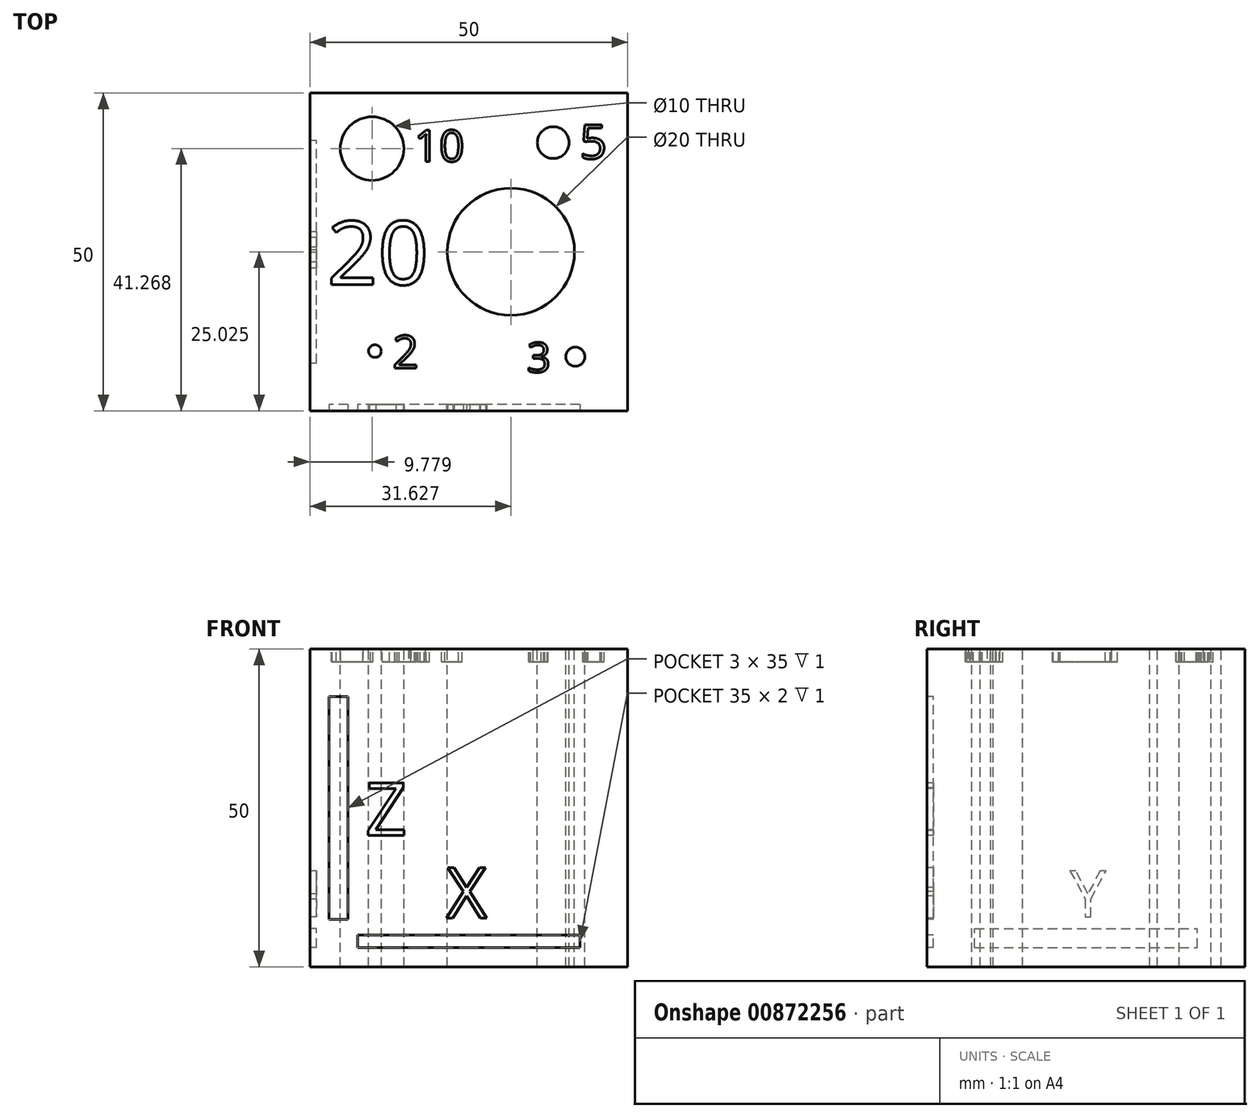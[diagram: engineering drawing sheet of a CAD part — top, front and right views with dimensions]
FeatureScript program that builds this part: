
annotation { "Feature Type Name" : "Feature", "Feature Type Description" : "" }
export const myFeature = defineFeature(function(context is Context, id is Id, definition is map)
    precondition{}
    {
        {
            var Q0;
            Q0=qCreatedBy(makeId("Top.planeOp"),FACE);
            var sketch = newSketch(context, id + "F0", { "sketchPlane" : qUnion([Q0])});
            skLineSegment(sketch, "E0.bottom", {"start": v(25, -25) * mm, "end": v(-25, -25) * mm});
            skLineSegment(sketch, "E0.top", {"start": v(25, 25) * mm, "end": v(-25, 25) * mm});
            skLineSegment(sketch, "E0.left", {"start": v(25, -25) * mm, "end": v(25, 25) * mm});
            skLineSegment(sketch, "E0.right", {"start": v(-25, -25) * mm, "end": v(-25, 25) * mm});
            skPoint(sketch, "E0.middle", {"position": v(0, 0) * mm});
            skSolve(sketch);
        }
        {
            var Q0;
            Q0 = qSketchRegion(id + "F0", true);
            extrude(context, id + "F1", {"entities" : qUnion([Q0]), "depth" : 50 * mm, "offsetDistance" : 25 * mm});
        }
        {
            var Q0;
            Q0=makeQuery(id+"F1.opExtrude","SWEPT_FACE",FACE,{"disambiguationData":[OSD([sQuery(id+"F0.wireOp",EDGE,"E0.bottom")])]});
            var sketch = newSketch(context, id + "F2", { "sketchPlane" : qUnion([Q0])});
            skLineSegment(sketch, "E1.bottom", {"start": v(17.5, 3) * mm, "end": v(-17.5, 3) * mm});
            skLineSegment(sketch, "E1.top", {"start": v(17.5, 5) * mm, "end": v(-17.5, 5) * mm});
            skLineSegment(sketch, "E1.left", {"start": v(17.5, 3) * mm, "end": v(17.5, 5) * mm});
            skLineSegment(sketch, "E1.right", {"start": v(-17.5, 3) * mm, "end": v(-17.5, 5) * mm});
            skPoint(sketch, "E1.middle", {"position": v(0, 4) * mm});
            skLineSegment(sketch, "E2.bottom", {"start": v(-19, 7.5) * mm, "end": v(-22, 7.5) * mm});
            skLineSegment(sketch, "E2.top", {"start": v(-19, 42.5) * mm, "end": v(-22, 42.5) * mm});
            skLineSegment(sketch, "E2.left", {"start": v(-19, 7.5) * mm, "end": v(-19, 42.5) * mm});
            skLineSegment(sketch, "E2.right", {"start": v(-22, 7.5) * mm, "end": v(-22, 42.5) * mm});
            skPoint(sketch, "E2.middle", {"position": v(-20.5, 25) * mm});
            skPoint(sketch, "E2.middle.positionSnap0", {"position": v(-25, 25) * mm});
            skPoint(sketch, "E2.centerSnap0", {"position": v(-25, 25) * mm});
            skText(sketch, "E3", { "text": "Z", "fontName": "OpenSans-Regular.ttf"});
            skText(sketch, "E4", { "text": "X", "fontName": "OpenSans-Regular.ttf"});
            skLineSegment(sketch, "E5", {"start": v(-25, 25) * mm, "end": v(25, 25) * mm, "construction": true});
            const initialGuessF2  = {"E3": [-0.01628, 0.02067, 1, 0, 0.0083], "E4": [-0.00355, 0.00767, 1, 0, 0.00801]};
            skSetInitialGuess(sketch, initialGuessF2);
            skSolve(sketch);
        }
        {
            var Q0;
            Q0=makeQuery(id+"F1.opExtrude","SWEPT_FACE",FACE,{"disambiguationData":[OSD([sQuery(id+"F0.wireOp",EDGE,"E0.right")])]});
            var sketch = newSketch(context, id + "F3", { "sketchPlane" : qUnion([Q0])});
            skLineSegment(sketch, "E6.bottom", {"start": v(17.5, 3) * mm, "end": v(-17.5, 3) * mm});
            skLineSegment(sketch, "E6.top", {"start": v(17.5, 6) * mm, "end": v(-17.5, 6) * mm});
            skLineSegment(sketch, "E6.left", {"start": v(17.5, 3) * mm, "end": v(17.5, 6) * mm});
            skLineSegment(sketch, "E6.right", {"start": v(-17.5, 3) * mm, "end": v(-17.5, 6) * mm});
            skPoint(sketch, "E6.middle", {"position": v(0, 4.5) * mm});
            skText(sketch, "E7", { "text": "Y", "fontName": "OpenSans-Regular.ttf"});
            const initialGuessF3  = {"E7": [-0.00318, 0.00785, 1, 0, 0.00733]};
            skSetInitialGuess(sketch, initialGuessF3);
            skSolve(sketch);
        }
        {
            var Q0;
            Q0 = qSketchRegion(id + "F2", true);
            extrude(context, id + "F4", {"entities" : qUnion([Q0]), "operationType" : NewBodyOperationType.REMOVE, "oppositeDirection" : true, "depth" : 1 * mm, "offsetDistance" : 25 * mm});
        }
        {
            var Q0;
            Q0=makeQuery(id+"F3.imprint","IMPRINT",FACE,{"disambiguationData":[TD([[makeQuery(id+"F3.imprint","IMPRINT",EDGE,{"derivedFrom":sQuery(id+"F3.wireOp",EDGE,"E7.sketch_text.stroke-0")}),-1.0]])]});
            var Q1;
            Q1=makeQuery(id+"F3.imprint","IMPRINT",FACE,{"disambiguationData":[TD([[makeQuery(id+"F3.imprint","IMPRINT",EDGE,{"derivedFrom":sQuery(id+"F3.wireOp",EDGE,"E6.bottom")}),-1.0]])]});
            extrude(context, id + "F5", {"entities" : qUnion([Q0, Q1]), "operationType" : NewBodyOperationType.REMOVE, "oppositeDirection" : true, "depth" : 1 * mm, "offsetDistance" : 25 * mm});
        }
        {
            var Q0;
            Q0=makeQuery(id+"F1.opExtrude","CAP_FACE",FACE,{"disambiguationData":[OSD([sQuery(id+"F0.wireOp",EDGE,"E0.bottom"),sQuery(id+"F0.wireOp",EDGE,"E0.top"),sQuery(id+"F0.wireOp",EDGE,"E0.left"),sQuery(id+"F0.wireOp",EDGE,"E0.right")])],"isStart":false});
            var sketch = newSketch(context, id + "F6", { "sketchPlane" : qUnion([Q0])});
            skCircle(sketch, "E8", {"center": v(6.63, 0.03) * mm, "radius": 10 * mm});
            skCircle(sketch, "E9", {"center": v(-15.22, 16.27) * mm, "radius": 5 * mm});
            skCircle(sketch, "E10", {"center": v(13.3, 17.2) * mm, "radius": 2.5 * mm});
            skCircle(sketch, "E11", {"center": v(16.76, -16.49) * mm, "radius": 1.5 * mm});
            skCircle(sketch, "E12", {"center": v(-14.78, -15.6) * mm, "radius": 1 * mm});
            skText(sketch, "E13", { "text": "10", "fontName": "OpenSans-Regular.ttf"});
            skText(sketch, "E14", { "text": "5", "fontName": "OpenSans-Regular.ttf"});
            skText(sketch, "E15", { "text": "2", "fontName": "OpenSans-Regular.ttf"});
            skText(sketch, "E16", { "text": "3", "fontName": "OpenSans-Regular.ttf"});
            skText(sketch, "E17", { "text": "20", "fontName": "OpenSans-Regular.ttf"});
            const initialGuessF6  = {"E13": [-0.0086, 0.01423, 1, 0, 0.00496], "E14": [0.01743, 0.01467, 1, 0, 0.0054], "E15": [-0.01202, -0.0183, 1, 0, 0.00518], "E16": [0.00915, -0.01892, 1, 0, 0.00469], "E17": [-0.02228, -0.00513, 1, 0, 0.01004]};
            skSetInitialGuess(sketch, initialGuessF6);
            skSolve(sketch);
        }
        {
            var Q0;
            Q0=makeQuery(id+"F6.imprint","IMPRINT",FACE,{"disambiguationData":[TD([[makeQuery(id+"F6.imprint","IMPRINT",EDGE,{"derivedFrom":sQuery(id+"F6.wireOp",EDGE,"E9")}),1.0]])]});
            var Q1;
            Q1=makeQuery(id+"F6.imprint","IMPRINT",FACE,{"disambiguationData":[TD([[makeQuery(id+"F6.imprint","IMPRINT",EDGE,{"derivedFrom":sQuery(id+"F6.wireOp",EDGE,"E8")}),1.0]])]});
            var Q2;
            Q2=makeQuery(id+"F6.imprint","IMPRINT",FACE,{"disambiguationData":[TD([[makeQuery(id+"F6.imprint","IMPRINT",EDGE,{"derivedFrom":sQuery(id+"F6.wireOp",EDGE,"E10")}),1.0]])]});
            var Q3;
            Q3=makeQuery(id+"F6.imprint","IMPRINT",FACE,{"disambiguationData":[TD([[makeQuery(id+"F6.imprint","IMPRINT",EDGE,{"derivedFrom":sQuery(id+"F6.wireOp",EDGE,"E11")}),1.0]])]});
            var Q4;
            Q4=makeQuery(id+"F6.imprint","IMPRINT",FACE,{"disambiguationData":[TD([[makeQuery(id+"F6.imprint","IMPRINT",EDGE,{"derivedFrom":sQuery(id+"F6.wireOp",EDGE,"E12")}),1.0]])]});
            extrude(context, id + "F7", {"entities" : qUnion([Q0, Q1, Q2, Q3, Q4]), "operationType" : NewBodyOperationType.REMOVE, "endBound" : BoundingType.UP_TO_NEXT, "oppositeDirection" : true, "depth" : 25 * mm, "offsetDistance" : 25 * mm});
        }
        {
            var Q0;
            Q0 = qSketchRegion(id + "F6", true);
            extrude(context, id + "F8", {"entities" : qUnion([Q0]), "operationType" : NewBodyOperationType.REMOVE, "oppositeDirection" : true, "depth" : 2 * mm, "offsetDistance" : 25 * mm});
        }
    });
